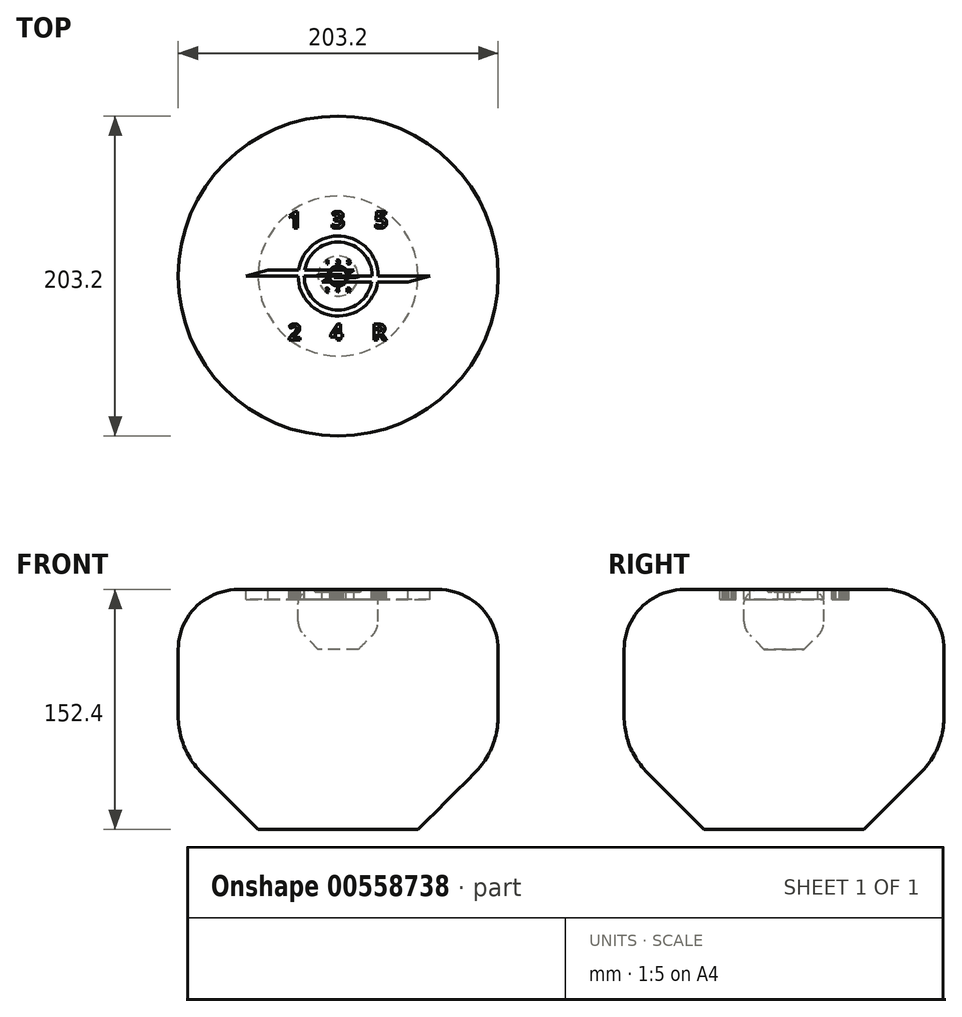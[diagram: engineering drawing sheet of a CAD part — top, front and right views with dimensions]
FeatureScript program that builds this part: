
annotation { "Feature Type Name" : "Feature", "Feature Type Description" : "" }
export const myFeature = defineFeature(function(context is Context, id is Id, definition is map)
    precondition{}
    {
        {
            var Q0;
            Q0=qCreatedBy(makeId("Top.planeOp"),FACE);
            var sketch = newSketch(context, id + "F0", { "sketchPlane" : qUnion([Q0])});
            skLineSegment(sketch, "E0", {"start": v(-44.45, 3.81) * mm, "end": v(-25.11, 3.81) * mm});
            skLineSegment(sketch, "E1", {"start": v(10.16, 3.81) * mm, "end": v(5.08, 0) * mm});
            skLineSegment(sketch, "E2", {"start": v(5.08, 0) * mm, "end": v(21.59, 0) * mm});
            skLineSegment(sketch, "E3", {"start": v(58.42, 0) * mm, "end": v(44.45, -3.8) * mm});
            skLineSegment(sketch, "E4", {"start": v(44.45, -3.8) * mm, "end": v(25.11, -3.8) * mm});
            skLineSegment(sketch, "E5", {"start": v(-10.16, -3.8) * mm, "end": v(-5.08, 0) * mm});
            skLineSegment(sketch, "E6", {"start": v(-5.08, 0) * mm, "end": v(-21.6, 0) * mm});
            skLineSegment(sketch, "E7", {"start": v(-58.42, 0) * mm, "end": v(-44.45, 3.81) * mm});
            skLineSegment(sketch, "E8", {"start": v(-21.25, 3.81) * mm, "end": v(10.16, 3.81) * mm});
            skLineSegment(sketch, "E9", {"start": v(-25.4, 0) * mm, "end": v(-58.42, 0) * mm});
            skArc(sketch, "E10", {"start": v(-21.6, 0) * mm, "mid": v(-1.91, -21.5) * mm, "end": v(21.25, -3.8) * mm});
            skArc(sketch, "E11", {"start": v(-25.4, 0) * mm, "mid": v(-1.91, -25.33) * mm, "end": v(25.11, -3.8) * mm});
            skLineSegment(sketch, "E12", {"start": v(25.4, 0) * mm, "end": v(58.42, 0) * mm});
            skLineSegment(sketch, "E13", {"start": v(21.25, -3.8) * mm, "end": v(-10.16, -3.8) * mm});
            skArc(sketch, "E14", {"start": v(21.59, 0) * mm, "mid": v(1.91, 21.5) * mm, "end": v(-21.25, 3.8) * mm});
            skArc(sketch, "E15", {"start": v(25.4, 0) * mm, "mid": v(1.91, 25.33) * mm, "end": v(-25.11, 3.81) * mm});
            skSolve(sketch);
        }
        {
            var Q0;
            Q0=qCreatedBy(makeId("Top.planeOp"),FACE);
            var sketch = newSketch(context, id + "F1", { "sketchPlane" : qUnion([Q0])});
            skCircle(sketch, "E16", {"center": v(0, 0) * mm, "radius": 101.6 * mm});
            skSolve(sketch);
        }
        {
            var Q0;
            Q0 = qSketchRegion(id + "F1", true);
            extrude(context, id + "F2", {"entities" : qUnion([Q0]), "oppositeDirection" : true, "depth" : 152.4 * mm, "offsetDistance" : 25.4 * mm});
        }
        {
            var Q0;
            Q0=makeQuery(id+"F2.opExtrude","CAP_EDGE",EDGE,{"disambiguationData":[OSD([sQuery(id+"F1.wireOp",EDGE,"E16")])],"isStart":true});
            fillet(context, id + "F3", {"entities" : qUnion([Q0]), "radius" : 38.1 * mm, "tangentPropagation" : true, "allowEdgeOverflow" : false});
        }
        {
            var Q0;
            Q0=makeQuery(id+"F2.opExtrude","CAP_EDGE",EDGE,{"disambiguationData":[OSD([sQuery(id+"F1.wireOp",EDGE,"E16")])],"isStart":false});
            chamfer(context, id + "F4", {"entities" : qUnion([Q0]), "width" : 50.8 * mm, "tangentPropagation" : true});
        }
        {
            var Q0;
            {var subQ0=sQuery(id+"F1.wireOp",EDGE,"E16");Q0=makeQuery(id+"F4.opChamfer","BLEND_EDGE",EDGE,{"blendedFrom":[makeQuery(id+"F2.opExtrude","CAP_EDGE",EDGE,{"disambiguationData":[OSD([subQ0])],"isStart":false}),makeQuery(id+"F2.opExtrude","SWEPT_FACE",FACE,{"disambiguationData":[OSD([subQ0])]})],"blendedInto":[makeQuery(id+"F2.opExtrude","SWEPT_FACE",FACE,{"disambiguationData":[OSD([subQ0])]})]});}
            fillet(context, id + "F5", {"entities" : qUnion([Q0]), "radius" : 50.8 * mm, "tangentPropagation" : true, "allowEdgeOverflow" : false});
        }
        {
            var Q0;
            Q0=qCreatedBy(makeId("Top.planeOp"),FACE);
            var sketch = newSketch(context, id + "F6", { "sketchPlane" : qUnion([Q0])});
            skText(sketch, "E17", { "text": "1     3     5", "fontName": "OpenSans-Bold.ttf"});
            skText(sketch, "E18", { "text": "2     4     R", "fontName": "OpenSans-Bold.ttf"});
            const initialGuessF6  = {"E17": [-0.03175, 0.03048, 1, 0, 0.01056], "E18": [-0.03175, -0.04072, 1, 0, 0.01024]};
            skSetInitialGuess(sketch, initialGuessF6);
            skSolve(sketch);
        }
        {
            var Q0;
            Q0 = qSketchRegion(id + "F0", true);
            var Q1;
            Q1 = qSketchRegion(id + "F6", true);
            extrude(context, id + "F7", {"entities" : qUnion([Q0, Q1]), "operationType" : NewBodyOperationType.REMOVE, "oppositeDirection" : true, "depth" : 6.35 * mm, "offsetDistance" : 25.4 * mm});
        }
        {
            var Q0;
            Q0=makeQuery(id+"F2.opExtrude","SWEPT_BODY",BODY,{"disambiguationData":[OSD([sQuery(id+"F1.wireOp",EDGE,"E16")])]});
            var Q1;
            Q1=qCreatedBy(makeId("Origin.pointOp"),VERTEX);
            transform(context, id + "F8", {"entities" : qUnion([Q0]), "transformType" : TransformType.SCALE_UNIFORMLY, "scale" : 0.25, "scalePoint" : qUnion([Q1]), "makeCopy" : true});
        }
    });
